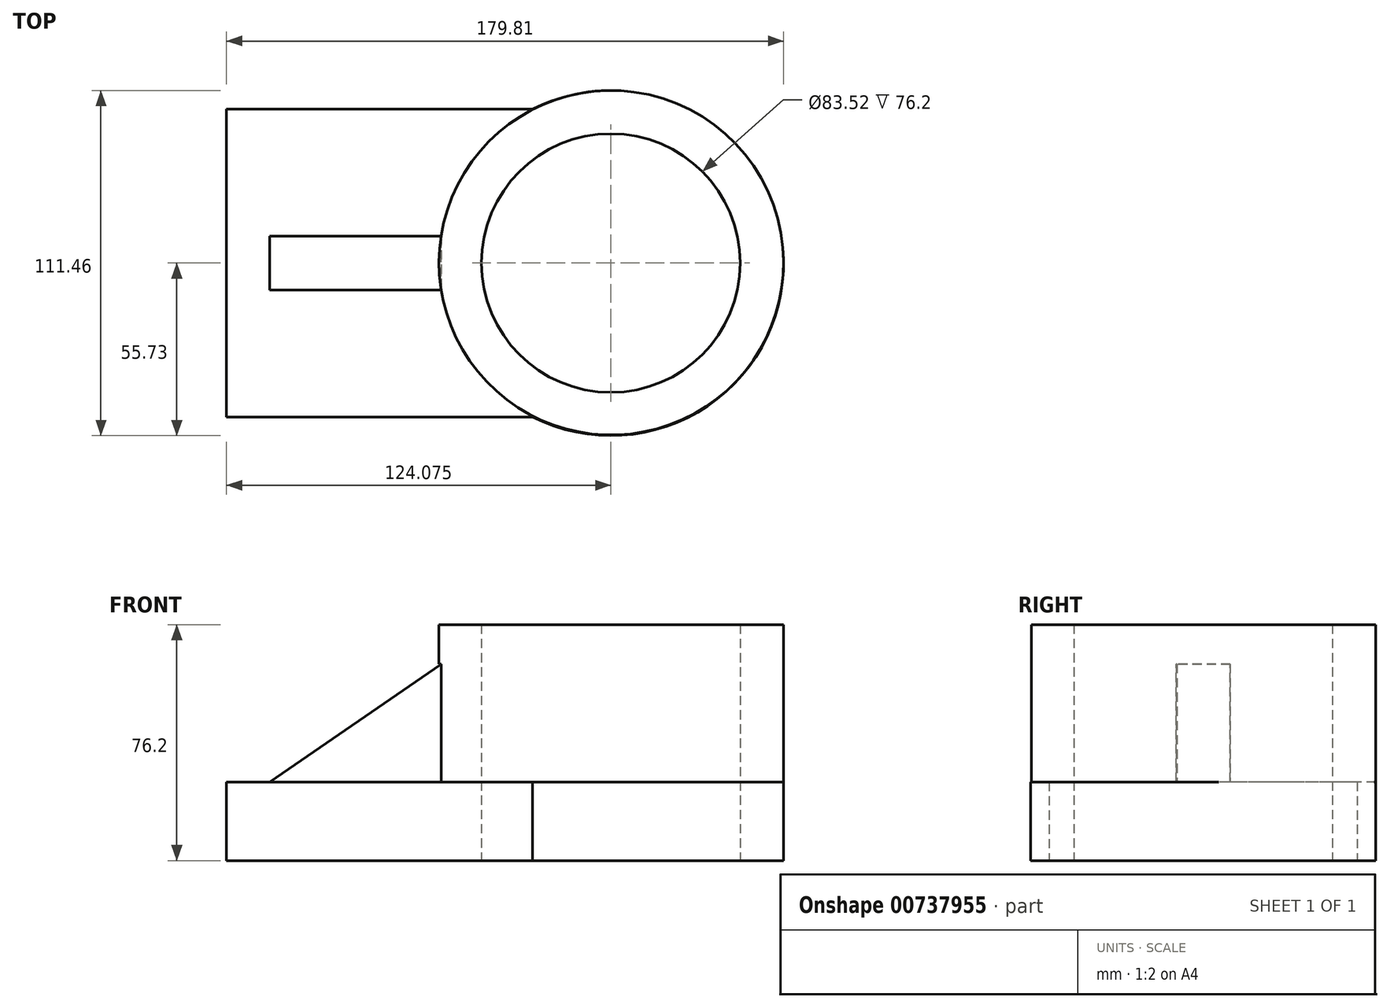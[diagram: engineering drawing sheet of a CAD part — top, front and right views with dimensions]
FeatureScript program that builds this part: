
annotation { "Feature Type Name" : "Feature", "Feature Type Description" : "" }
export const myFeature = defineFeature(function(context is Context, id is Id, definition is map)
    precondition{}
    {
        {
            var Q0;
            Q0=qCreatedBy(makeId("Top.planeOp"),FACE);
            var sketch = newSketch(context, id + "F0", { "sketchPlane" : qUnion([Q0])});
            skLineSegment(sketch, "E0.bottom", {"start": v(62.04, 49.68) * mm, "end": v(-62.04, 49.68) * mm});
            skLineSegment(sketch, "E0.top", {"start": v(62.04, -49.68) * mm, "end": v(-62.04, -49.68) * mm});
            skLineSegment(sketch, "E0.left", {"start": v(62.04, 49.68) * mm, "end": v(62.04, -49.68) * mm});
            skLineSegment(sketch, "E0.right", {"start": v(-62.04, 49.68) * mm, "end": v(-62.04, -49.68) * mm});
            skPoint(sketch, "E0.middle", {"position": v(0, 0) * mm});
            skCircle(sketch, "E1", {"center": v(62.04, 0) * mm, "radius": 55.73 * mm});
            skCircle(sketch, "E2", {"center": v(62.04, 0) * mm, "radius": 41.76 * mm});
            skSolve(sketch);
        }
        {
            var Q0;
            {var subQ0=sQuery(id+"F0.wireOp",EDGE,"E0.right");Q0=makeQuery(id+"F0.imprint","IMPRINT",FACE,{"disambiguationData":[TD([[makeQuery(id+"F0.imprint","IMPRINT",EDGE,{"derivedFrom":subQ0}),1.0]])]});}
            extrude(context, id + "F1", {"entities" : qUnion([Q0]), "depth" : 25.4 * mm, "offsetDistance" : 25.4 * mm});
        }
        {
            var Q0;
            Q0 = qSketchRegion(id + "F0", true);
            extrude(context, id + "F2", {"entities" : qUnion([Q0]), "operationType" : NewBodyOperationType.ADD, "depth" : 76.2 * mm, "offsetDistance" : 25.4 * mm});
        }
        {
            var Q0;
            Q0=makeQuery(id+"F2.opExtrude","CAP_FACE",FACE,{"disambiguationData":[OSD([sQuery(id+"F0.wireOp",EDGE,"E0.bottom"),sQuery(id+"F0.wireOp",EDGE,"E0.top"),sQuery(id+"F0.wireOp",EDGE,"E0.right"),sQuery(id+"F0.wireOp",EDGE,"E1"),sQuery(id+"F0.wireOp",EDGE,"E2")])],"isStart":false});
            var sketch = newSketch(context, id + "F3", { "sketchPlane" : qUnion([Q0])});
            skCircle(sketch, "E3", {"center": v(62.15, 0.11) * mm, "radius": 55.6 * mm});
            skPoint(sketch, "E3.first.point", {"position": v(117.54, 5.04) * mm});
            skPoint(sketch, "E3.second.point", {"position": v(6.87, -5.8) * mm});
            skPoint(sketch, "E3.third.point", {"position": v(69.52, 55.23) * mm});
            skSolve(sketch);
        }
        {
            var Q0;
            {var subQ1=makeQuery(id+"F2.opExtrude","CAP_EDGE",EDGE,{"disambiguationData":[OSD([sQuery(id+"F0.wireOp",EDGE,"E0.bottom")])],"isStart":false});Q0=makeQuery(id+"F3.imprint","IMPRINT",FACE,{"disambiguationData":[TD([[makeQuery(id+"F3.imprint","IMPRINT",EDGE,{"derivedFrom":subQ1}),1.0]])]});}
            extrude(context, id + "F4", {"entities" : qUnion([Q0]), "operationType" : NewBodyOperationType.REMOVE, "oppositeDirection" : true, "depth" : 50.8 * mm, "offsetDistance" : 25.4 * mm});
        }
        {
            var Q0;
            Q0=makeQuery(id+"F4.boolean.opBoolean","COPY",FACE,{"derivedFrom":makeQuery(id+"F4.opExtrude","CAP_FACE",FACE,{"disambiguationData":[OSD([sQuery(id+"F0.wireOp",EDGE,"E0.bottom"),sQuery(id+"F0.wireOp",EDGE,"E0.top"),sQuery(id+"F0.wireOp",EDGE,"E0.right"),sQuery(id+"F0.wireOp",EDGE,"E1"),sQuery(id+"F3.wireOp",EDGE,"E3")])],"isStart":false})});
            var sketch = newSketch(context, id + "F5", { "sketchPlane" : qUnion([Q0])});
            skLineSegment(sketch, "E4.bottom", {"start": v(7.22, 8.75) * mm, "end": v(-48.17, 8.75) * mm});
            skLineSegment(sketch, "E4.top", {"start": v(7.22, -8.75) * mm, "end": v(-48.17, -8.75) * mm});
            skLineSegment(sketch, "E4.left", {"start": v(7.22, 8.75) * mm, "end": v(7.22, -8.75) * mm});
            skLineSegment(sketch, "E4.right", {"start": v(-48.17, 8.75) * mm, "end": v(-48.17, -8.75) * mm});
            skPoint(sketch, "E4.middle", {"position": v(-20.47, 0) * mm});
            skSolve(sketch);
        }
        {
            var Q0;
            {var subQ4=sQuery(id+"F5.wireOp",EDGE,"E4.bottom");Q0=makeQuery(id+"F5.imprint","IMPRINT",FACE,{"disambiguationData":[TD([[makeQuery(id+"F5.imprint","IMPRINT",EDGE,{"derivedFrom":subQ4}),1.0]])]});}
            extrude(context, id + "F6", {"entities" : qUnion([Q0]), "operationType" : NewBodyOperationType.ADD, "depth" : 38.1 * mm, "offsetDistance" : 25.4 * mm});
        }
        {
            var Q0;
            Q0=makeQuery(id+"F6.opExtrude","SWEPT_FACE",FACE,{"disambiguationData":[OSD([sQuery(id+"F5.wireOp",EDGE,"E4.top")])]});
            var sketch = newSketch(context, id + "F7", { "sketchPlane" : qUnion([Q0])});
            skSolve(sketch);
        }
        {
            var Q0;
            {var subQ0=sQuery(id+"F5.wireOp",EDGE,"E4.top");Q0=makeQuery(id+"F7.imprint","IMPRINT",FACE,{"disambiguationData":[TD([[makeQuery(id+"F7.imprint","IMPRINT",EDGE,{"derivedFrom":makeQuery(id+"F6.opExtrude","CAP_EDGE",EDGE,{"disambiguationData":[OSD([subQ0])],"isStart":false})}),1.0]])]});}
            var sketch = newSketch(context, id + "F8", { "sketchPlane" : qUnion([Q0])});
            skLineSegment(sketch, "E5", {"start": v(-48.17, 25.4) * mm, "end": v(7.1, 63.3) * mm});
            skLineSegment(sketch, "E6", {"start": v(7.1, 63.3) * mm, "end": v(7.22, 63.5) * mm});
            skLineSegment(sketch, "E7", {"start": v(7.22, 63.5) * mm, "end": v(7.1, 63.3) * mm});
            skSolve(sketch);
        }
        {
            var Q0;
            {var subQ0=sQuery(id+"F5.wireOp",EDGE,"E4.top");var subQ1=makeQuery(id+"F7.imprint","IMPRINT",EDGE,{"derivedFrom":makeQuery(id+"F6.opExtrude","CAP_EDGE",EDGE,{"disambiguationData":[OSD([subQ0])],"isStart":false})});Q0=makeQuery(id+"F8.imprint","IMPRINT",FACE,{"disambiguationData":[TD([[makeQuery(id+"F8.imprint","IMPRINT",EDGE,{"derivedFrom":subQ1}),1.0]])]});}
            extrude(context, id + "F9", {"entities" : qUnion([Q0]), "operationType" : NewBodyOperationType.REMOVE, "oppositeDirection" : true, "depth" : 50.8 * mm, "offsetDistance" : 25.4 * mm});
        }
    });
